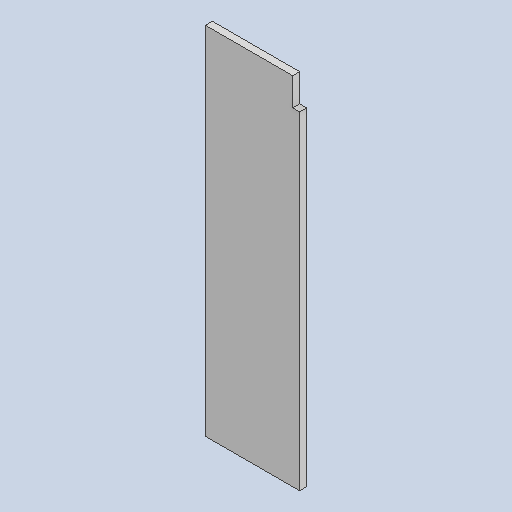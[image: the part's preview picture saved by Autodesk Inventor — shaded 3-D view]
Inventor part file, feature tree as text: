
AUTODESK INVENTOR PART (.ipt)
format: ipt  version: 2025 (Build 290162010, 162A)  size: 155,648 bytes
history: native  units: mm
features: sheet_metal_op x1, sketch x1, other x1
ambient origin geometry x8: Origin, YZ Plane, XZ Plane, XY Plane, X Axis, Y Axis, Z Axis, Center Point
bodies: Solid1 (feature_tree)
feature tree (3):
  sheet_metal_op  "Face1"
  sketch  "Sketch1"  dims[d15=2.0mm d27=27.0mm d29=102.0mm d30=2.0mm d31=8.0mm]
  other  "Plate1"
